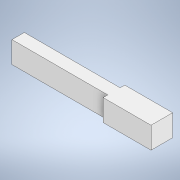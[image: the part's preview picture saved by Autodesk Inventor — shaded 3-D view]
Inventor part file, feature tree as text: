
AUTODESK INVENTOR PART (.ipt)
format: ipt  version: 2021 (Build 250183000, 183)  size: 99,840 bytes
history: native  units: in
note: dims shown in document units (in); Inventor stores cm internally (conversion verified against a paired STEP export)
features: extrude x1, sketch x1
ambient origin geometry x8: Origin, YZ Plane, XZ Plane, XY Plane, X Axis, Y Axis, Z Axis, Center Point
bodies: Solid1 (feature_tree)
feature tree (2):
  extrude  "Extrusion1"  Depth=5.8125in
  sketch  "Sketch1"  dims[d0=0.875in d1=5.8125in d2=3.875in d4=0.6875in d5=0.6875in d6=0.875in d7=0.0in]
